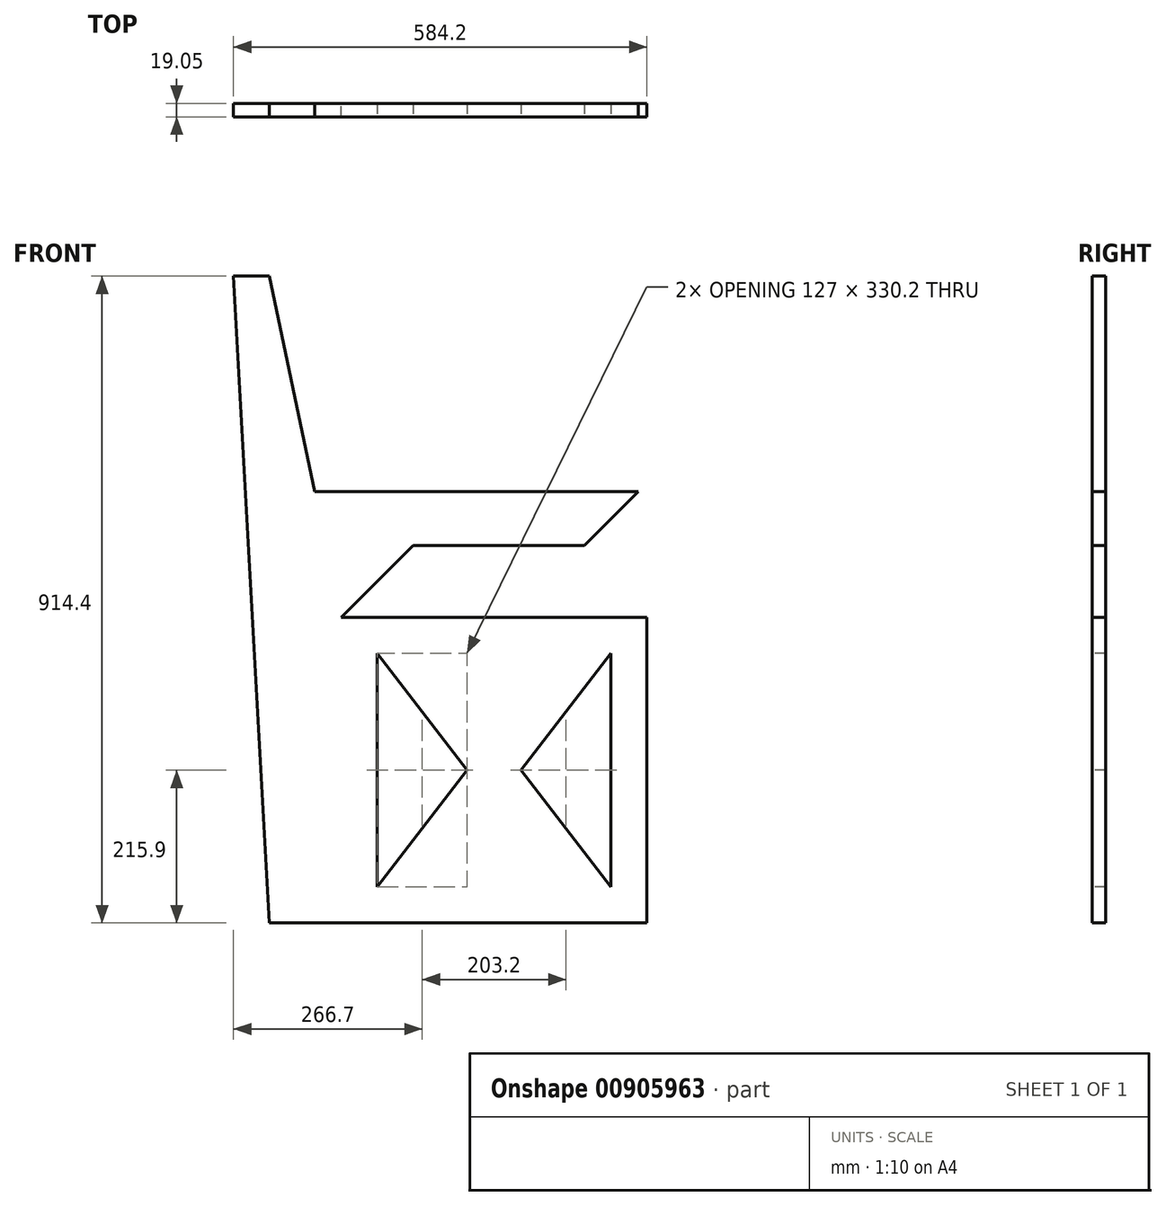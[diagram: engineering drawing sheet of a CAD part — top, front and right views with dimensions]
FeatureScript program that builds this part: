
annotation { "Feature Type Name" : "Feature", "Feature Type Description" : "" }
export const myFeature = defineFeature(function(context is Context, id is Id, definition is map)
    precondition{}
    {
        {
            var Q0;
            Q0=qCreatedBy(makeId("Front.planeOp"),FACE);
            var sketch = newSketch(context, id + "F0", { "sketchPlane" : qUnion([Q0])});
            skLineSegment(sketch, "E0.bottom", {"start": v(0, 0) * mm, "end": v(431.8, 0) * mm});
            skLineSegment(sketch, "E0.top", {"start": v(0, 431.8) * mm, "end": v(431.8, 431.8) * mm});
            skLineSegment(sketch, "E0.left", {"start": v(0, 0) * mm, "end": v(0, 431.8) * mm});
            skLineSegment(sketch, "E0.right", {"start": v(431.8, 0) * mm, "end": v(431.8, 431.8) * mm});
            skSolve(sketch);
        }
        {
            var Q0;
            Q0=makeQuery(id+"F0.imprint","IMPRINT",FACE,{"disambiguationData":[TD([[makeQuery(id+"F0.imprint","IMPRINT",EDGE,{"derivedFrom":sQuery(id+"F0.wireOp",EDGE,"E0.bottom")}),1.0]])]});
            extrude(context, id + "F1", {"entities" : qUnion([Q0]), "depth" : 19.05 * mm, "offsetDistance" : 25.4 * mm});
        }
        {
            var Q0;
            Q0=makeQuery(id+"F1.opExtrude","CAP_FACE",FACE,{"disambiguationData":[OSD([sQuery(id+"F0.wireOp",EDGE,"E0.bottom"),sQuery(id+"F0.wireOp",EDGE,"E0.top"),sQuery(id+"F0.wireOp",EDGE,"E0.left"),sQuery(id+"F0.wireOp",EDGE,"E0.right")])],"isStart":false});
            var sketch = newSketch(context, id + "F2", { "sketchPlane" : qUnion([Q0])});
            skLineSegment(sketch, "E1", {"start": v(50.8, 381) * mm, "end": v(50.8, 50.8) * mm});
            skLineSegment(sketch, "E2", {"start": v(50.8, 50.8) * mm, "end": v(177.8, 215.9) * mm});
            skLineSegment(sketch, "E3", {"start": v(177.8, 215.9) * mm, "end": v(50.8, 381) * mm});
            skLineSegment(sketch, "E4", {"start": v(381, 381) * mm, "end": v(381, 50.8) * mm});
            skLineSegment(sketch, "E5", {"start": v(381, 50.8) * mm, "end": v(254, 215.9) * mm});
            skLineSegment(sketch, "E6", {"start": v(254, 215.9) * mm, "end": v(381, 381) * mm});
            skSolve(sketch);
        }
        {
            var Q0;
            Q0=makeQuery(id+"F2.imprint","IMPRINT",FACE,{"disambiguationData":[TD([[makeQuery(id+"F2.imprint","IMPRINT",EDGE,{"derivedFrom":sQuery(id+"F2.wireOp",EDGE,"E1")}),1.0]])]});
            var Q1;
            Q1=makeQuery(id+"F2.imprint","IMPRINT",FACE,{"disambiguationData":[TD([[makeQuery(id+"F2.imprint","IMPRINT",EDGE,{"derivedFrom":sQuery(id+"F2.wireOp",EDGE,"E4")}),-1.0]])]});
            extrude(context, id + "F3", {"entities" : qUnion([Q0, Q1]), "operationType" : NewBodyOperationType.REMOVE, "endBound" : BoundingType.THROUGH_ALL, "oppositeDirection" : true, "depth" : 25.4 * mm, "offsetDistance" : 25.4 * mm});
        }
        {
            var Q0;
            Q0=makeQuery(id+"F1.opExtrude","CAP_FACE",FACE,{"disambiguationData":[OSD([sQuery(id+"F0.wireOp",EDGE,"E0.bottom"),sQuery(id+"F0.wireOp",EDGE,"E0.top"),sQuery(id+"F0.wireOp",EDGE,"E0.left"),sQuery(id+"F0.wireOp",EDGE,"E0.right")])],"isStart":false});
            var sketch = newSketch(context, id + "F4", { "sketchPlane" : qUnion([Q0])});
            skLineSegment(sketch, "E7", {"start": v(0, 431.8) * mm, "end": v(-101.6, 914.4) * mm});
            skLineSegment(sketch, "E8", {"start": v(-101.6, 914.4) * mm, "end": v(-152.4, 914.4) * mm});
            skLineSegment(sketch, "E9", {"start": v(-152.4, 914.4) * mm, "end": v(-152.4, 0) * mm});
            skLineSegment(sketch, "E10", {"start": v(-152.4, 0) * mm, "end": v(0, 0) * mm});
            skLineSegment(sketch, "E11", {"start": v(0, 0) * mm, "end": v(0, 431.8) * mm});
            skSolve(sketch);
        }
        {
            var Q0;
            Q0 = qSketchRegion(id + "F4", true);
            var Q1;
            Q1=makeQuery(id+"F1.opExtrude","CAP_FACE",FACE,{"disambiguationData":[OSD([sQuery(id+"F0.wireOp",EDGE,"E0.bottom"),sQuery(id+"F0.wireOp",EDGE,"E0.top"),sQuery(id+"F0.wireOp",EDGE,"E0.left"),sQuery(id+"F0.wireOp",EDGE,"E0.right")])],"isStart":true});
            extrude(context, id + "F5", {"entities" : qUnion([Q0]), "operationType" : NewBodyOperationType.ADD, "endBound" : BoundingType.UP_TO_SURFACE, "oppositeDirection" : true, "depth" : 25.4 * mm, "endBoundEntityFace" : qUnion([Q1]), "offsetDistance" : 25.4 * mm});
        }
        {
            var Q0;
            Q0=makeQuery(id+"F5.boolean.opBoolean","MERGE",FACE,{"derivedFrom":[makeQuery(id+"F1.opExtrude","CAP_FACE",FACE,{"disambiguationData":[OSD([sQuery(id+"F0.wireOp",EDGE,"E0.bottom"),sQuery(id+"F0.wireOp",EDGE,"E0.top"),sQuery(id+"F0.wireOp",EDGE,"E0.left"),sQuery(id+"F0.wireOp",EDGE,"E0.right")])],"isStart":false}),makeQuery(id+"F5.opExtrude","CAP_FACE",FACE,{"disambiguationData":[OSD([sQuery(id+"F4.wireOp",EDGE,"E7"),sQuery(id+"F4.wireOp",EDGE,"E8"),sQuery(id+"F4.wireOp",EDGE,"E9"),sQuery(id+"F4.wireOp",EDGE,"E10"),sQuery(id+"F4.wireOp",EDGE,"E11")])],"isStart":true})]});
            var sketch = newSketch(context, id + "F6", { "sketchPlane" : qUnion([Q0])});
            skLineSegment(sketch, "E12", {"start": v(-152.4, 914.4) * mm, "end": v(-152.4, 0) * mm});
            skLineSegment(sketch, "E13", {"start": v(-101.6, 0) * mm, "end": v(-152.4, 914.4) * mm});
            skLineSegment(sketch, "E14", {"start": v(-152.4, 0) * mm, "end": v(-101.6, 0) * mm});
            skLineSegment(sketch, "E15", {"start": v(431.8, 431.8) * mm, "end": v(381, 0) * mm});
            skSolve(sketch);
        }
        {
            var Q0;
            Q0 = qSketchRegion(id + "F6", true);
            extrude(context, id + "F7", {"entities" : qUnion([Q0]), "operationType" : NewBodyOperationType.REMOVE, "endBound" : BoundingType.THROUGH_ALL, "oppositeDirection" : true, "depth" : 25.4 * mm, "offsetDistance" : 25.4 * mm});
        }
        {
            var Q0;
            Q0=makeQuery(id+"F5.boolean.opBoolean","MERGE",FACE,{"derivedFrom":[makeQuery(id+"F1.opExtrude","CAP_FACE",FACE,{"disambiguationData":[OSD([sQuery(id+"F0.wireOp",EDGE,"E0.bottom"),sQuery(id+"F0.wireOp",EDGE,"E0.top"),sQuery(id+"F0.wireOp",EDGE,"E0.left"),sQuery(id+"F0.wireOp",EDGE,"E0.right")])],"isStart":false}),makeQuery(id+"F5.opExtrude","CAP_FACE",FACE,{"disambiguationData":[OSD([sQuery(id+"F4.wireOp",EDGE,"E7"),sQuery(id+"F4.wireOp",EDGE,"E8"),sQuery(id+"F4.wireOp",EDGE,"E9"),sQuery(id+"F4.wireOp",EDGE,"E10"),sQuery(id+"F4.wireOp",EDGE,"E11")])],"isStart":true})]});
            var sketch = newSketch(context, id + "F8", { "sketchPlane" : qUnion([Q0])});
            skLineSegment(sketch, "E16", {"start": v(-37.43, 609.6) * mm, "end": v(419.77, 609.6) * mm});
            skLineSegment(sketch, "E17", {"start": v(419.77, 609.6) * mm, "end": v(343.57, 533.4) * mm});
            skLineSegment(sketch, "E18", {"start": v(0, 431.8) * mm, "end": v(-37.43, 609.6) * mm});
            skLineSegment(sketch, "E19", {"start": v(0, 431.8) * mm, "end": v(101.6, 533.4) * mm});
            skLineSegment(sketch, "E20", {"start": v(101.6, 533.4) * mm, "end": v(343.57, 533.4) * mm});
            skSolve(sketch);
        }
        {
            var Q0;
            Q0 = qSketchRegion(id + "F8", true);
            extrude(context, id + "F9", {"entities" : qUnion([Q0]), "operationType" : NewBodyOperationType.ADD, "oppositeDirection" : true, "depth" : 19.05 * mm, "offsetDistance" : 25.4 * mm});
        }
    });
